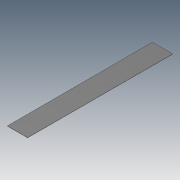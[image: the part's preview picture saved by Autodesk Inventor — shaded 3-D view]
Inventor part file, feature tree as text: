
AUTODESK INVENTOR PART (.ipt)
format: ipt  version: 2020 (Build 240168000, 168)  size: 78,848 bytes
history: native  units: mm
features: other x1, extrude x1, sketch x1
ambient origin geometry x8: Origin, YZ Plane, XZ Plane, XY Plane, X Axis, Y Axis, Z Axis, Center Point
bodies: Body1 (feature_tree)
feature tree (3):
  other  "ソリッド1"
  extrude  "押し出し1"  Depth=1500.0mm
  sketch  "スケッチ1"
